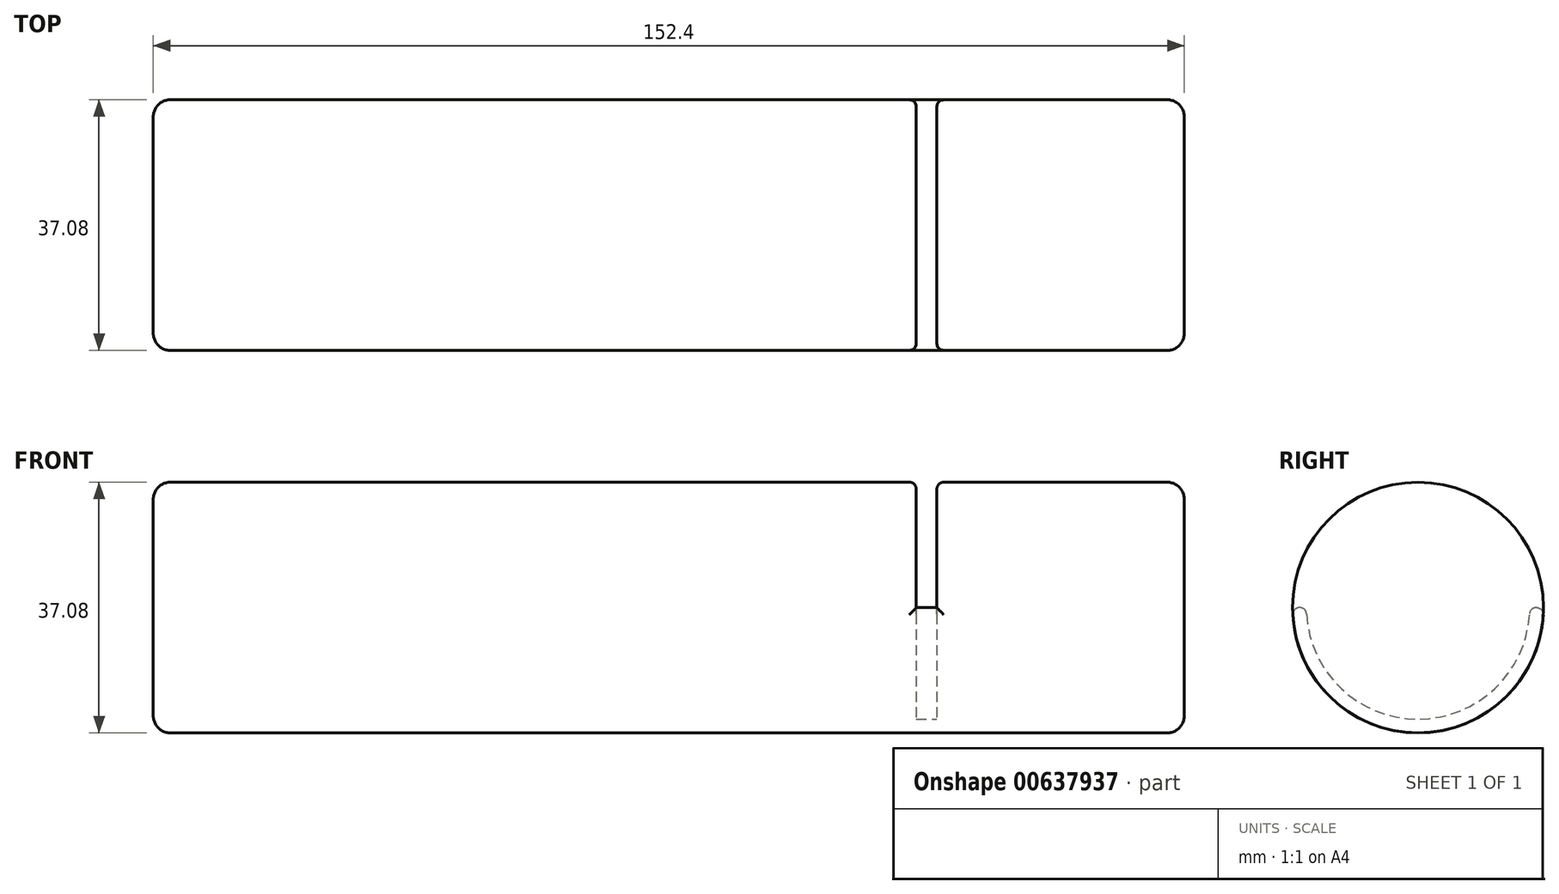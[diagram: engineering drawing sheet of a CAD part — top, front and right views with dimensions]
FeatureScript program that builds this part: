
annotation { "Feature Type Name" : "Feature", "Feature Type Description" : "" }
export const myFeature = defineFeature(function(context is Context, id is Id, definition is map)
    precondition{}
    {
        {
            var Q0;
            Q0=qCreatedBy(makeId("Right.planeOp"),FACE);
            var sketch = newSketch(context, id + "F0", { "sketchPlane" : qUnion([Q0])});
            skCircle(sketch, "E0", {"center": v(0, 0) * mm, "radius": 18.54 * mm});
            skSolve(sketch);
        }
        {
            var Q0;
            Q0 = qSketchRegion(id + "F0", true);
            extrude(context, id + "F1", {"entities" : qUnion([Q0]), "endBound" : BoundingType.SYMMETRIC, "depth" : 152.4 * mm, "offsetDistance" : 25.4 * mm});
        }
        {
            var Q0;
            Q0=qCreatedBy(makeId("Right.planeOp"),FACE);
            cPlane(context, id + "F2", {"entities" : qUnion([Q0]), "cplaneType" : CPlaneType.OFFSET, "offset" : 38.1 * mm, "width" : 152.4 * mm, "height" : 152.4 * mm});
        }
        {
            var Q0;
            Q0=qCreatedBy(id+"F2.planeOp",FACE);
            var sketch = newSketch(context, id + "F3", { "sketchPlane" : qUnion([Q0])});
            skArc(sketch, "E1", {"start": v(-16.51, 0) * mm, "mid": v(0, -16.51) * mm, "end": v(16.51, 0) * mm});
            skLineSegment(sketch, "E2", {"start": v(-16.51, 0) * mm, "end": v(-22.12, 0) * mm});
            skLineSegment(sketch, "E3", {"start": v(-22.12, 0) * mm, "end": v(-22.12, 25.24) * mm});
            skLineSegment(sketch, "E4", {"start": v(-22.12, 25.24) * mm, "end": v(22.24, 22.2) * mm});
            skLineSegment(sketch, "E5", {"start": v(22.24, 22.2) * mm, "end": v(22.9, 0) * mm});
            skLineSegment(sketch, "E6", {"start": v(22.9, 0) * mm, "end": v(16.51, 0) * mm});
            skSolve(sketch);
        }
        {
            var Q0;
            Q0 = qSketchRegion(id + "F3", true);
            extrude(context, id + "F4", {"entities" : qUnion([Q0]), "operationType" : NewBodyOperationType.REMOVE, "endBound" : BoundingType.SYMMETRIC, "oppositeDirection" : true, "depth" : 3.05 * mm, "offsetDistance" : 25.4 * mm});
        }
        {
            var Q0;
            Q0=makeQuery(id+"F4.boolean.opBoolean","INTERSECT",EDGE,{"derivedFrom":[makeQuery(id+"F1.opExtrude","SWEPT_FACE",FACE,{"disambiguationData":[OSD([sQuery(id+"F0.wireOp",EDGE,"E0")])]}),makeQuery(id+"F4.opExtrude","CAP_FACE",FACE,{"disambiguationData":[OSD([sQuery(id+"F3.wireOp",EDGE,"E1"),sQuery(id+"F3.wireOp",EDGE,"E2"),sQuery(id+"F3.wireOp",EDGE,"E3"),sQuery(id+"F3.wireOp",EDGE,"E4"),sQuery(id+"F3.wireOp",EDGE,"E5"),sQuery(id+"F3.wireOp",EDGE,"E6")])],"isStart":false})]});
            var Q1;
            Q1=makeQuery(id+"F4.boolean.opBoolean","INTERSECT",EDGE,{"derivedFrom":[makeQuery(id+"F1.opExtrude","SWEPT_FACE",FACE,{"disambiguationData":[OSD([sQuery(id+"F0.wireOp",EDGE,"E0")])]}),makeQuery(id+"F4.opExtrude","CAP_FACE",FACE,{"disambiguationData":[OSD([sQuery(id+"F3.wireOp",EDGE,"E1"),sQuery(id+"F3.wireOp",EDGE,"E2"),sQuery(id+"F3.wireOp",EDGE,"E3"),sQuery(id+"F3.wireOp",EDGE,"E4"),sQuery(id+"F3.wireOp",EDGE,"E5"),sQuery(id+"F3.wireOp",EDGE,"E6")])],"isStart":true})]});
            var Q2;
            Q2=makeQuery(id+"F4.boolean.opBoolean","INTERSECT",EDGE,{"derivedFrom":[makeQuery(id+"F1.opExtrude","SWEPT_FACE",FACE,{"disambiguationData":[OSD([sQuery(id+"F0.wireOp",EDGE,"E0")])]}),makeQuery(id+"F4.opExtrude","SWEPT_FACE",FACE,{"disambiguationData":[OSD([sQuery(id+"F3.wireOp",EDGE,"E2")])]})]});
            var Q3;
            Q3=makeQuery(id+"F4.boolean.opBoolean","INTERSECT",EDGE,{"derivedFrom":[makeQuery(id+"F1.opExtrude","SWEPT_FACE",FACE,{"disambiguationData":[OSD([sQuery(id+"F0.wireOp",EDGE,"E0")])]}),makeQuery(id+"F4.opExtrude","SWEPT_FACE",FACE,{"disambiguationData":[OSD([sQuery(id+"F3.wireOp",EDGE,"E6")])]})]});
            var Q4;
            Q4=makeQuery(id+"F4.boolean.opBoolean","COPY",EDGE,{"derivedFrom":makeQuery(id+"F4.opExtrude","SWEPT_EDGE",EDGE,{"disambiguationData":[OSD([sQuery(id+"F3.wireOp",EDGE,"E1"),sQuery(id+"F3.wireOp",EDGE,"E2")])]})});
            var Q5;
            Q5=makeQuery(id+"F4.boolean.opBoolean","COPY",EDGE,{"derivedFrom":makeQuery(id+"F4.opExtrude","SWEPT_EDGE",EDGE,{"disambiguationData":[OSD([sQuery(id+"F3.wireOp",EDGE,"E1"),sQuery(id+"F3.wireOp",EDGE,"E6")])]})});
            fillet(context, id + "F5", {"entities" : qUnion([Q0, Q1, Q2, Q3, Q4, Q5]), "radius" : 1.02 * mm, "tangentPropagation" : true, "allowEdgeOverflow" : false});
        }
        {
            var Q0;
            Q0=qCreatedBy(makeId("Right.planeOp"),FACE);
            cPlane(context, id + "F6", {"entities" : qUnion([Q0]), "cplaneType" : CPlaneType.OFFSET, "offset" : 19.05 * mm, "width" : 152.4 * mm, "height" : 152.4 * mm});
        }
        {
            var Q0;
            Q0=makeQuery(id+"F1.opExtrude","CAP_EDGE",EDGE,{"disambiguationData":[OSD([sQuery(id+"F0.wireOp",EDGE,"E0")])],"isStart":true});
            var Q1;
            Q1=makeQuery(id+"F1.opExtrude","CAP_EDGE",EDGE,{"disambiguationData":[OSD([sQuery(id+"F0.wireOp",EDGE,"E0")])],"isStart":false});
            fillet(context, id + "F7", {"entities" : qUnion([Q0, Q1]), "radius" : 2.54 * mm, "tangentPropagation" : true, "allowEdgeOverflow" : false});
        }
    });
